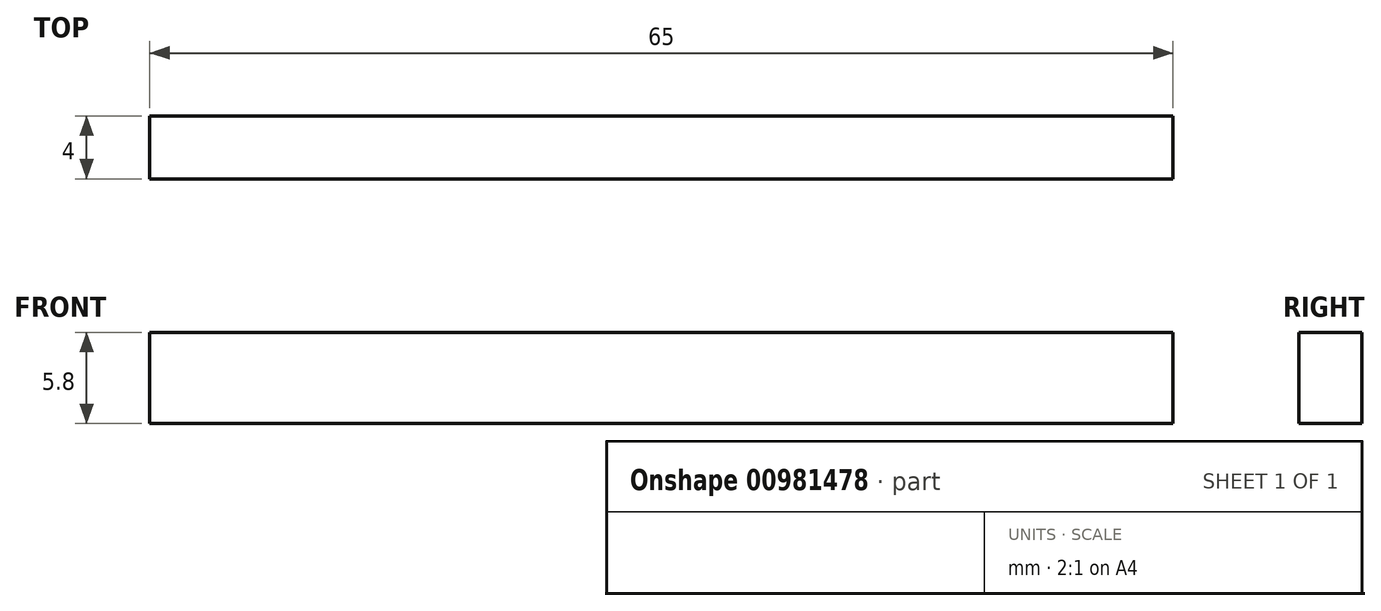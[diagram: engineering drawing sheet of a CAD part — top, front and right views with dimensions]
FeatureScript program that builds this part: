
annotation { "Feature Type Name" : "Feature", "Feature Type Description" : "" }
export const myFeature = defineFeature(function(context is Context, id is Id, definition is map)
    precondition{}
    {
        {
            var Q0;
            Q0=qCreatedBy(makeId("Top.planeOp"),FACE);
            var sketch = newSketch(context, id + "F0", { "sketchPlane" : qUnion([Q0])});
            skLineSegment(sketch, "E0.bottom", {"start": v(-31.9, 9.2) * mm, "end": v(33.1, 9.2) * mm});
            skLineSegment(sketch, "E0.top", {"start": v(-31.9, 5.2) * mm, "end": v(33.1, 5.2) * mm});
            skLineSegment(sketch, "E0.left", {"start": v(-31.9, 9.2) * mm, "end": v(-31.9, 5.2) * mm});
            skLineSegment(sketch, "E0.right", {"start": v(33.1, 9.2) * mm, "end": v(33.1, 5.2) * mm});
            skSolve(sketch);
        }
        {
            var Q0;
            Q0=makeQuery(id+"F0.imprint","IMPRINT",FACE,{"disambiguationData":[TD([[makeQuery(id+"F0.imprint","IMPRINT",EDGE,{"derivedFrom":sQuery(id+"F0.wireOp",EDGE,"E0.bottom")}),-1.0]])]});
            extrude(context, id + "F1", {"entities" : qUnion([Q0]), "depth" : 5.8 * mm, "offsetDistance" : 25 * mm});
        }
    });
